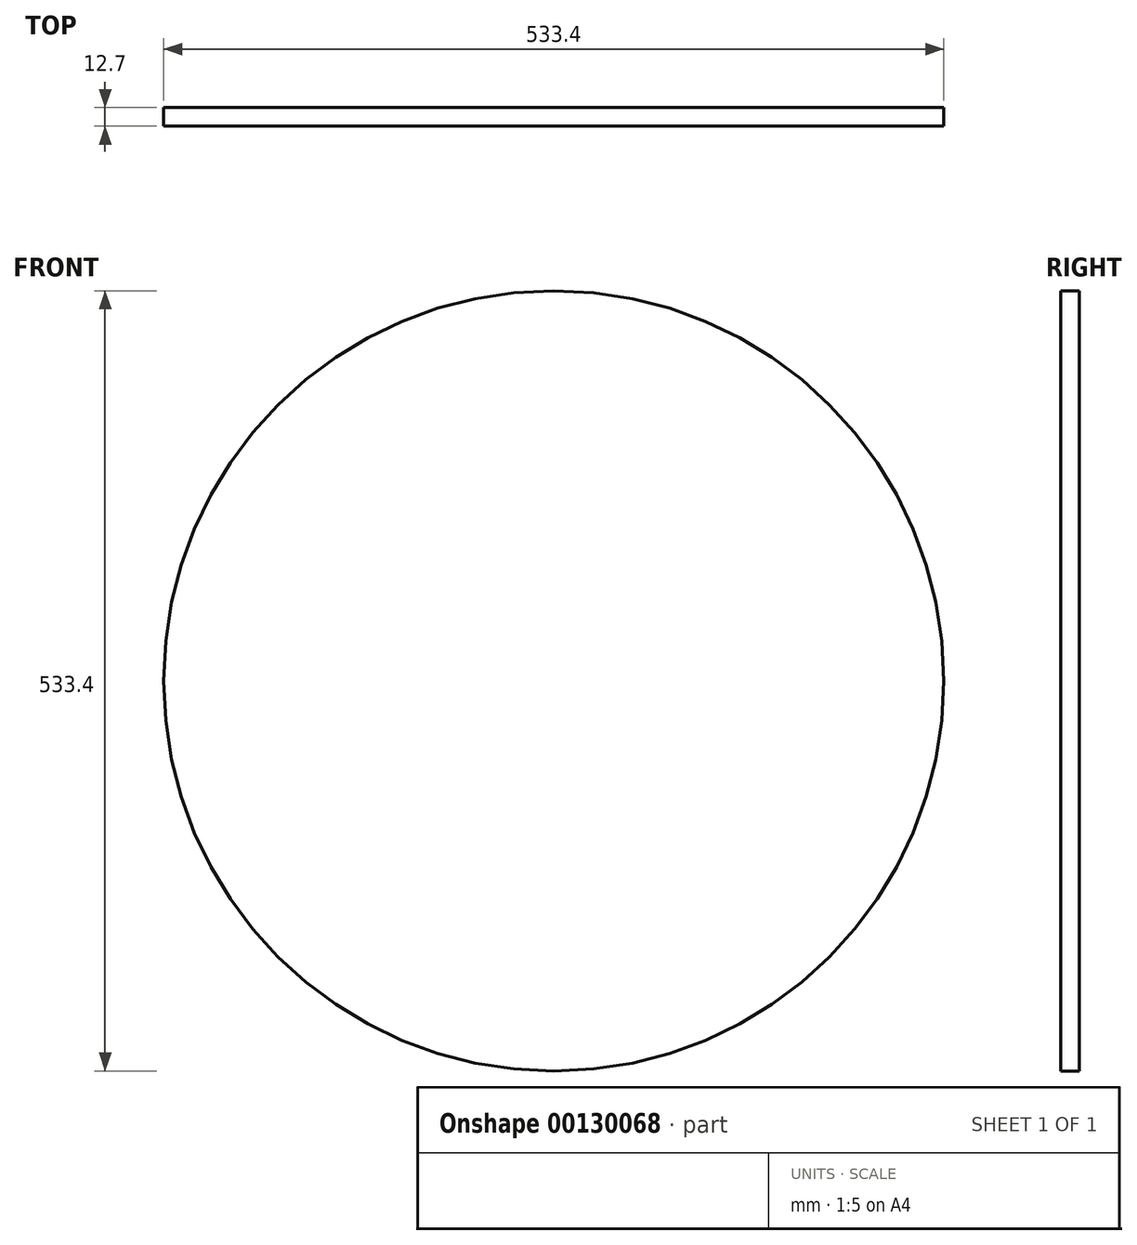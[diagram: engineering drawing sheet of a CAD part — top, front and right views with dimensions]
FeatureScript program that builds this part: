
annotation { "Feature Type Name" : "Feature", "Feature Type Description" : "" }
export const myFeature = defineFeature(function(context is Context, id is Id, definition is map)
    precondition{}
    {
        {
            var Q0;
            Q0=qCreatedBy(makeId("Front.planeOp"),FACE);
            var sketch = newSketch(context, id + "F0", { "sketchPlane" : qUnion([Q0])});
            skCircle(sketch, "E0", {"center": v(-10.03, 18) * mm, "radius": 266.7 * mm});
            skSolve(sketch);
        }
        {
            var Q0;
            Q0 = qSketchRegion(id + "F0", true);
            extrude(context, id + "F1", {"entities" : qUnion([Q0]), "depth" : 12.7 * mm});
        }
    });
